# Revit family: ASL_Door Suite_Stile_100mm
name_source: partatom
category: Detail Items
revit_build: Autodesk Revit 2018 (Build: 20170223_1515(x64)
units: mm (PartAtom-declared; Revit-internal decimal feet)

## family parameters
Rotate with component = No
Section Shape = Not Defined
Shared = Yes

## types (3) — shared parameters
Infill for Closing Stile = No
Manufacturer = Aluminate Solutions Limited
Technical Info = www.aluminate.nz

## per-type parameters (varying)
| type | 100mm Close Stile | 100mm Hinge Stile | 100mm Lockset Stile | ASL_Woolpile_1 | ASL_Woolpile_2 | ASL_Woolpile_Closing Stile_Sliding | Type Comments |
| Hinge Stile Hinge Door 100mm | No | Yes | No | No | No | No | ASL Door Suite 100mm Hinge Stile Hinge Door |
| Closing Stile Sliding Door 100mm | Yes | No | No | No | No | Yes | ASL Door Suite 100mm Closing Stile Sliding Door |
| Lockset Stile Double Action Hinge, Pviot and Sliding Door 100mm | No | No | Yes | Yes | Yes | No | ASL Door Suite 100mm Lockset Stile Double Action Hinge, Pviot and Sliding Door |

## geometry (parser evidence)
native form markers: Sweep x5
no freeform markers — native parametric forms only
